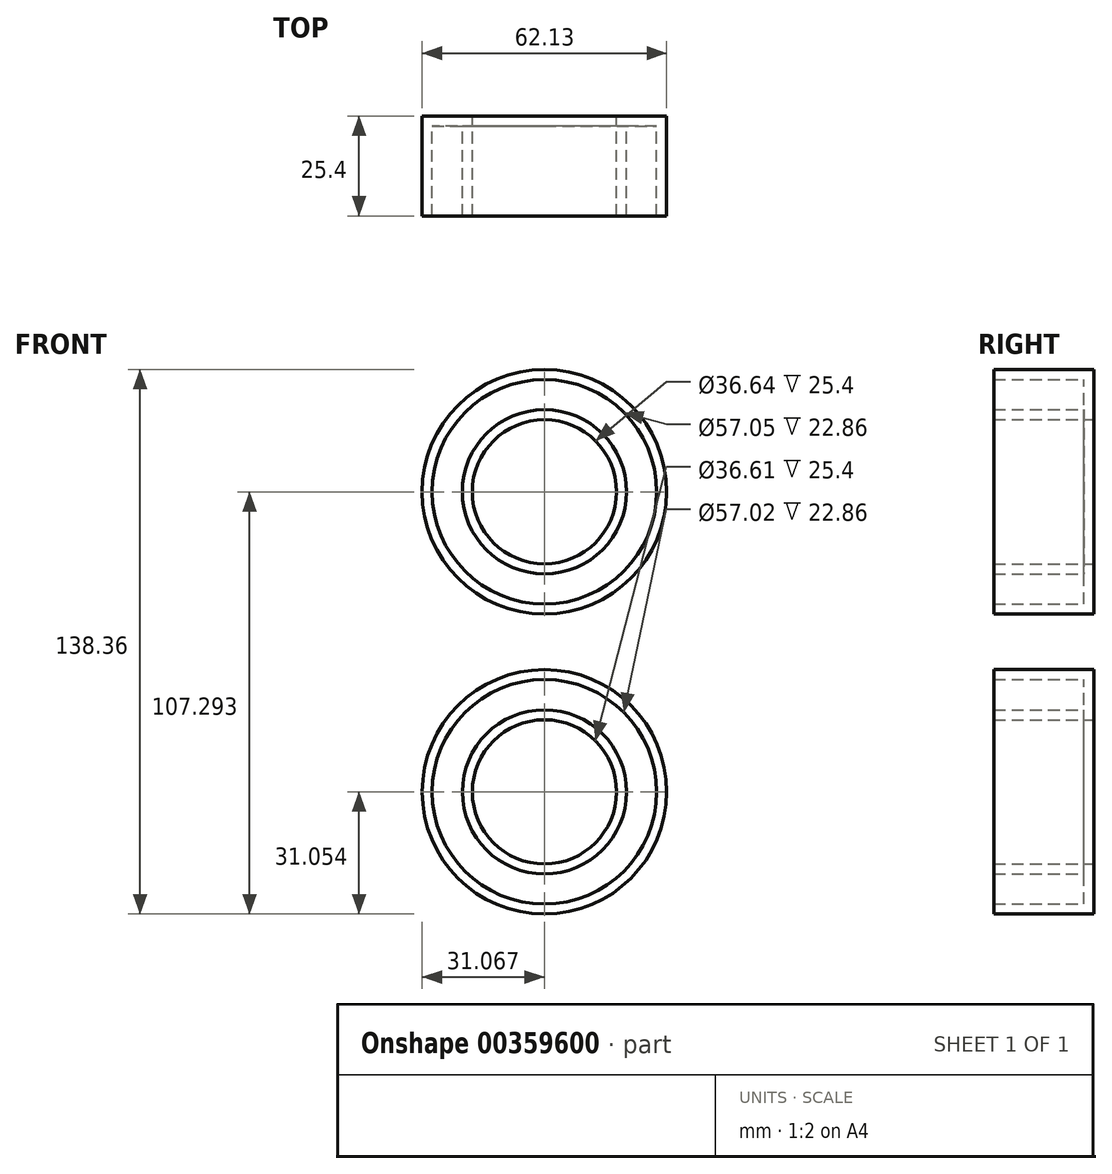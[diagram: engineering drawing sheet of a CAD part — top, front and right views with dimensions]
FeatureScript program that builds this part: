
annotation { "Feature Type Name" : "Feature", "Feature Type Description" : "" }
export const myFeature = defineFeature(function(context is Context, id is Id, definition is map)
    precondition{}
    {
        {
            var Q0;
            Q0=qCreatedBy(makeId("Front.planeOp"),FACE);
            var sketch = newSketch(context, id + "F0", { "sketchPlane" : qUnion([Q0])});
            skCircle(sketch, "E0", {"center": v(-38.52, 38.8) * mm, "radius": 31.06 * mm});
            skCircle(sketch, "E1", {"center": v(-38.52, -37.45) * mm, "radius": 31.05 * mm});
            skCircle(sketch, "E2", {"center": v(-38.52, 38.8) * mm, "radius": 18.32 * mm});
            skCircle(sketch, "E3", {"center": v(-38.52, -37.45) * mm, "radius": 18.3 * mm});
            skSolve(sketch);
        }
        {
            var Q0;
            Q0 = qSketchRegion(id + "F0", true);
            extrude(context, id + "F1", {"entities" : qUnion([Q0]), "depth" : 25.4 * mm});
        }
        {
            var Q0;
            Q0=makeQuery(id+"F1.opExtrude","CAP_FACE",FACE,{"disambiguationData":[OSD([sQuery(id+"F0.wireOp",EDGE,"E0"),sQuery(id+"F0.wireOp",EDGE,"E2")])],"isStart":false});
            var Q1;
            Q1=makeQuery(id+"F1.opExtrude","CAP_FACE",FACE,{"disambiguationData":[OSD([sQuery(id+"F0.wireOp",EDGE,"E1"),sQuery(id+"F0.wireOp",EDGE,"E3")])],"isStart":false});
            shell(context, id + "F2", {"entities" : qUnion([Q0, Q1]), "thickness" : 2.54 * mm});
        }
    });
